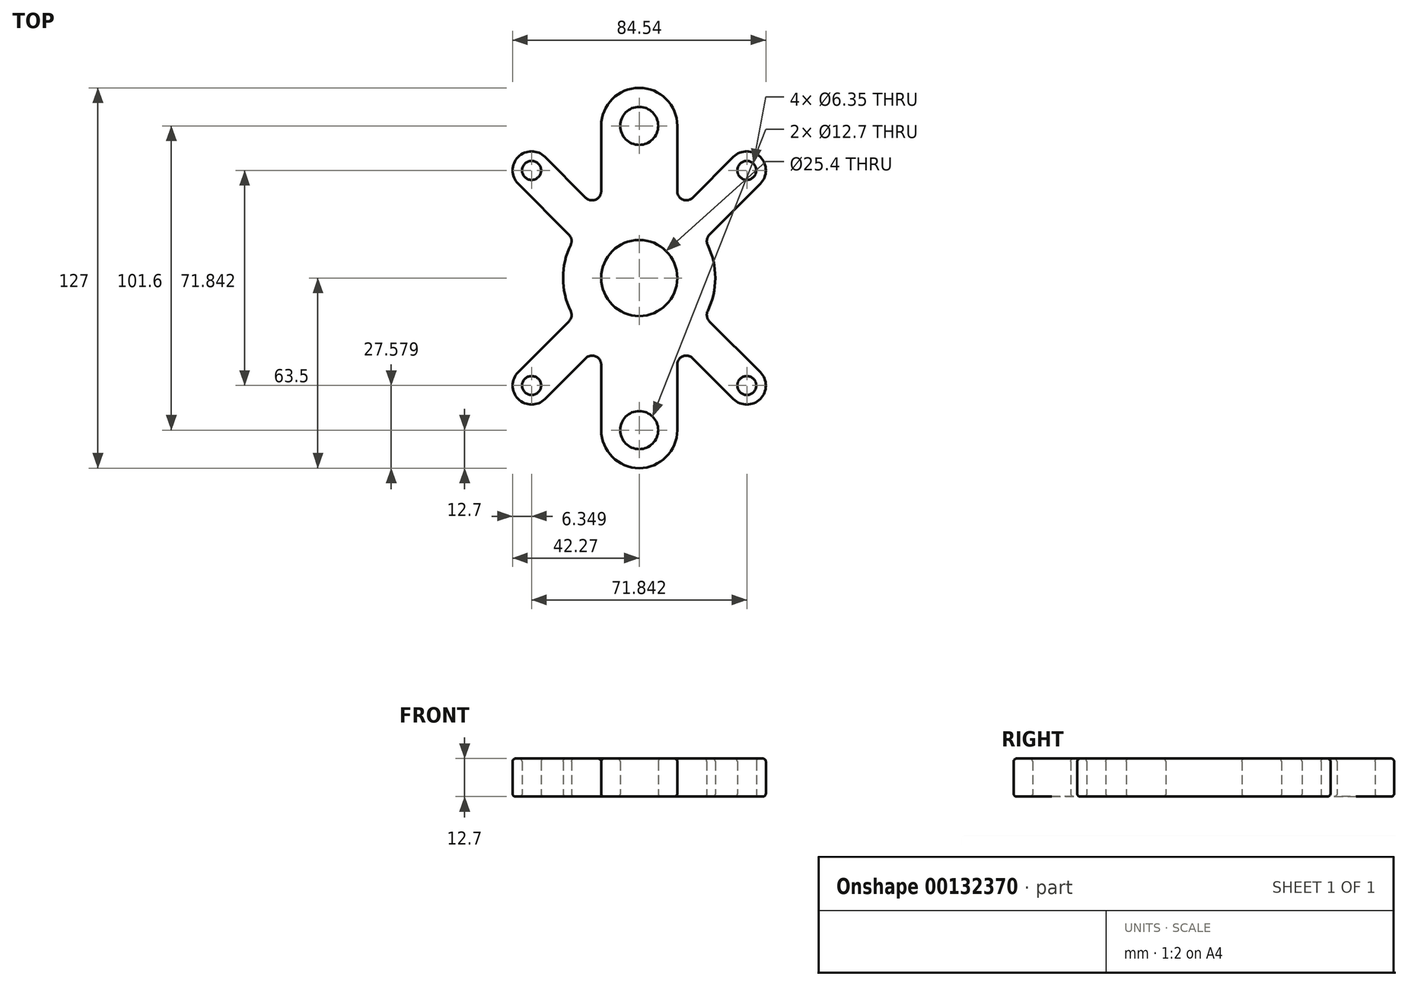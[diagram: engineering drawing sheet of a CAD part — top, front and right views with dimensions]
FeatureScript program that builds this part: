
annotation { "Feature Type Name" : "Feature", "Feature Type Description" : "" }
export const myFeature = defineFeature(function(context is Context, id is Id, definition is map)
    precondition{}
    {
        {
            var Q0;
            Q0=qCreatedBy(makeId("Top.planeOp"),FACE);
            var sketch = newSketch(context, id + "F0", { "sketchPlane" : qUnion([Q0])});
            skArc(sketch, "E0", {"start": v(-12.7, 22) * mm, "mid": v(-12.8, 21.94) * mm, "end": v(-12.9, 21.88) * mm});
            skCircle(sketch, "E1", {"center": v(0, 0) * mm, "radius": 12.7 * mm});
            skLineSegment(sketch, "E2", {"start": v(0, 0) * mm, "end": v(0, 50.8) * mm, "construction": true});
            skArc(sketch, "E3", {"start": v(12.7, 50.8) * mm, "mid": v(0, 63.5) * mm, "end": v(-12.7, 50.8) * mm});
            skCircle(sketch, "E4", {"center": v(0, 50.8) * mm, "radius": 6.35 * mm});
            skLineSegment(sketch, "E5", {"start": v(0, 0) * mm, "end": v(-35.92, 35.92) * mm, "construction": true});
            skLineSegment(sketch, "E6", {"start": v(35.92, -35.92) * mm, "end": v(0, 0) * mm, "construction": true});
            skLineSegment(sketch, "E7.MirrorCS", {"start": v(0, 0) * mm, "end": v(35.92, 35.92) * mm, "construction": true});
            skLineSegment(sketch, "E8.MirrorCS", {"start": v(-35.92, -35.92) * mm, "end": v(0, 0) * mm, "construction": true});
            skArc(sketch, "E9", {"start": v(-31.43, 40.41) * mm, "mid": v(-40.41, 40.41) * mm, "end": v(-40.41, 31.43) * mm});
            skArc(sketch, "E10", {"start": v(40.41, 31.43) * mm, "mid": v(40.41, 40.41) * mm, "end": v(31.43, 40.41) * mm});
            skArc(sketch, "E11", {"start": v(31.43, -40.41) * mm, "mid": v(40.41, -40.41) * mm, "end": v(40.41, -31.43) * mm});
            skArc(sketch, "E12", {"start": v(-40.41, -31.43) * mm, "mid": v(-40.41, -40.41) * mm, "end": v(-31.43, -40.41) * mm});
            skCircle(sketch, "E13", {"center": v(-35.92, 35.92) * mm, "radius": 3.17 * mm});
            skCircle(sketch, "E14", {"center": v(35.92, 35.92) * mm, "radius": 3.17 * mm});
            skCircle(sketch, "E15", {"center": v(35.92, -35.92) * mm, "radius": 3.17 * mm});
            skCircle(sketch, "E16", {"center": v(-35.92, -35.92) * mm, "radius": 3.17 * mm});
            skLineSegment(sketch, "E17", {"start": v(-12.7, 50.8) * mm, "end": v(-12.7, 28.92) * mm});
            skLineSegment(sketch, "E18", {"start": v(12.7, 50.8) * mm, "end": v(12.7, 28.92) * mm});
            skLineSegment(sketch, "E19", {"start": v(31.43, 40.41) * mm, "end": v(17.82, 26.8) * mm});
            skLineSegment(sketch, "E20", {"start": v(40.41, 31.43) * mm, "end": v(23.45, 14.47) * mm});
            skLineSegment(sketch, "E21", {"start": v(-31.43, 40.41) * mm, "end": v(-17.82, 26.8) * mm});
            skLineSegment(sketch, "E22", {"start": v(-40.41, 31.43) * mm, "end": v(-23.45, 14.47) * mm});
            skLineSegment(sketch, "E23", {"start": v(-31.43, -40.41) * mm, "end": v(-17.82, -26.8) * mm});
            skLineSegment(sketch, "E24", {"start": v(-40.41, -31.43) * mm, "end": v(-23.45, -14.47) * mm});
            skLineSegment(sketch, "E25", {"start": v(31.43, -40.41) * mm, "end": v(17.82, -26.8) * mm});
            skLineSegment(sketch, "E26", {"start": v(40.41, -31.43) * mm, "end": v(23.45, -14.47) * mm});
            skArc(sketch, "E27.trimOffspring", {"start": v(12.9, 21.88) * mm, "mid": v(12.8, 21.94) * mm, "end": v(12.7, 22) * mm});
            skArc(sketch, "E28.trimOffspring", {"start": v(-22.87, 11.05) * mm, "mid": v(-25.4, 0) * mm, "end": v(-22.87, -11.05) * mm});
            skArc(sketch, "E29.trimOffspring", {"start": v(22.87, -11.05) * mm, "mid": v(25.4, 0) * mm, "end": v(22.87, 11.05) * mm});
            skArc(sketch, "E30.filletArc", {"start": v(-17.82, 26.8) * mm, "mid": v(-14.55, 26.15) * mm, "end": v(-12.7, 28.92) * mm});
            skPoint(sketch, "E31.visualSharp", {"position": v(-21.88, 12.9) * mm});
            skArc(sketch, "E31.filletArc", {"start": v(-22.87, 11.05) * mm, "mid": v(-22.62, 12.85) * mm, "end": v(-23.45, 14.47) * mm});
            skArc(sketch, "E32.filletArc", {"start": v(12.7, 28.92) * mm, "mid": v(14.55, 26.15) * mm, "end": v(17.82, 26.8) * mm});
            skPoint(sketch, "E33.visualSharp", {"position": v(21.88, 12.9) * mm});
            skArc(sketch, "E33.filletArc", {"start": v(23.45, 14.47) * mm, "mid": v(22.62, 12.85) * mm, "end": v(22.87, 11.05) * mm});
            skPoint(sketch, "E34.visualSharp", {"position": v(21.88, -12.9) * mm});
            skArc(sketch, "E34.filletArc", {"start": v(22.87, -11.05) * mm, "mid": v(22.62, -12.85) * mm, "end": v(23.45, -14.47) * mm});
            skPoint(sketch, "E35.visualSharp", {"position": v(12.9, -21.88) * mm});
            skPoint(sketch, "E36.visualSharp", {"position": v(-12.9, -21.88) * mm});
            skPoint(sketch, "E37.visualSharp", {"position": v(-21.88, -12.9) * mm});
            skArc(sketch, "E37.filletArc", {"start": v(-23.45, -14.47) * mm, "mid": v(-22.62, -12.85) * mm, "end": v(-22.87, -11.05) * mm});
            skLineSegment(sketch, "E38", {"start": v(-25.4, 0) * mm, "end": v(25.4, 0) * mm, "construction": true});
            skArc(sketch, "E39.MirrorCS", {"start": v(12.7, -50.8) * mm, "mid": v(0, -63.5) * mm, "end": v(-12.7, -50.8) * mm});
            skCircle(sketch, "E40.MirrorC", {"center": v(0, -50.8) * mm, "radius": 6.35 * mm});
            skLineSegment(sketch, "E41.MirrorCS", {"start": v(0, 0) * mm, "end": v(0, -50.8) * mm, "construction": true});
            skLineSegment(sketch, "E42", {"start": v(-12.7, -50.8) * mm, "end": v(-12.7, -28.92) * mm});
            skLineSegment(sketch, "E43", {"start": v(12.7, -50.8) * mm, "end": v(12.7, -28.92) * mm});
            skArc(sketch, "E44.filletArc", {"start": v(-12.7, -28.92) * mm, "mid": v(-14.55, -26.15) * mm, "end": v(-17.82, -26.8) * mm});
            skArc(sketch, "E45.filletArc", {"start": v(17.82, -26.8) * mm, "mid": v(14.55, -26.15) * mm, "end": v(12.7, -28.92) * mm});
            skSolve(sketch);
        }
        {
            var Q0;
            Q0=makeQuery(id+"F0.imprint","IMPRINT",FACE,{"disambiguationData":[TD([[makeQuery(id+"F0.imprint","IMPRINT",EDGE,{"derivedFrom":sQuery(id+"F0.wireOp",EDGE,"E1")}),-1.0]])]});
            extrude(context, id + "F1", {"entities" : qUnion([Q0]), "depth" : 12.7 * mm});
        }
        {
            var Q0;
            Q0=makeQuery(id+"F1.opExtrude","CAP_FACE",FACE,{"disambiguationData":[OSD([sQuery(id+"F0.wireOp",EDGE,"E1"),sQuery(id+"F0.wireOp",EDGE,"E3"),sQuery(id+"F0.wireOp",EDGE,"E4"),sQuery(id+"F0.wireOp",EDGE,"E9"),sQuery(id+"F0.wireOp",EDGE,"E10"),sQuery(id+"F0.wireOp",EDGE,"E11"),sQuery(id+"F0.wireOp",EDGE,"E12"),sQuery(id+"F0.wireOp",EDGE,"E13"),sQuery(id+"F0.wireOp",EDGE,"E14"),sQuery(id+"F0.wireOp",EDGE,"E15"),sQuery(id+"F0.wireOp",EDGE,"E16"),sQuery(id+"F0.wireOp",EDGE,"E17"),sQuery(id+"F0.wireOp",EDGE,"E18"),sQuery(id+"F0.wireOp",EDGE,"E19"),sQuery(id+"F0.wireOp",EDGE,"E20"),sQuery(id+"F0.wireOp",EDGE,"E21"),sQuery(id+"F0.wireOp",EDGE,"E22"),sQuery(id+"F0.wireOp",EDGE,"E23"),sQuery(id+"F0.wireOp",EDGE,"E24"),sQuery(id+"F0.wireOp",EDGE,"E25"),sQuery(id+"F0.wireOp",EDGE,"E26"),sQuery(id+"F0.wireOp",EDGE,"E28.trimOffspring"),sQuery(id+"F0.wireOp",EDGE,"E29.trimOffspring"),sQuery(id+"F0.wireOp",EDGE,"E30.filletArc"),sQuery(id+"F0.wireOp",EDGE,"E31.filletArc"),sQuery(id+"F0.wireOp",EDGE,"E32.filletArc"),sQuery(id+"F0.wireOp",EDGE,"E33.filletArc"),sQuery(id+"F0.wireOp",EDGE,"E34.filletArc"),sQuery(id+"F0.wireOp",EDGE,"E37.filletArc"),sQuery(id+"F0.wireOp",EDGE,"E39.MirrorCS"),sQuery(id+"F0.wireOp",EDGE,"E40.MirrorC"),sQuery(id+"F0.wireOp",EDGE,"E42"),sQuery(id+"F0.wireOp",EDGE,"E43"),sQuery(id+"F0.wireOp",EDGE,"E44.filletArc"),sQuery(id+"F0.wireOp",EDGE,"E45.filletArc")])],"isStart":false});
            var Q1;
            Q1=makeQuery(id+"F1.opExtrude","SWEPT_FACE",FACE,{"disambiguationData":[OSD([sQuery(id+"F0.wireOp",EDGE,"E43")])]});
            var Q2;
            Q2=makeQuery(id+"F1.opExtrude","SWEPT_FACE",FACE,{"disambiguationData":[OSD([sQuery(id+"F0.wireOp",EDGE,"E39.MirrorCS")])]});
            var Q3;
            Q3=makeQuery(id+"F1.opExtrude","SWEPT_FACE",FACE,{"disambiguationData":[OSD([sQuery(id+"F0.wireOp",EDGE,"E44.filletArc")])]});
            var Q4;
            Q4=makeQuery(id+"F1.opExtrude","SWEPT_FACE",FACE,{"disambiguationData":[OSD([sQuery(id+"F0.wireOp",EDGE,"E30.filletArc")])]});
            var Q5;
            Q5=makeQuery(id+"F1.opExtrude","CAP_EDGE",EDGE,{"disambiguationData":[OSD([sQuery(id+"F0.wireOp",EDGE,"E25")])],"isStart":false});
            var Q6;
            Q6=makeQuery(id+"F1.opExtrude","CAP_EDGE",EDGE,{"disambiguationData":[OSD([sQuery(id+"F0.wireOp",EDGE,"E25")])],"isStart":true});
            var Q7;
            Q7=makeQuery(id+"F1.opExtrude","CAP_EDGE",EDGE,{"disambiguationData":[OSD([sQuery(id+"F0.wireOp",EDGE,"E17")])],"isStart":false});
            var Q8;
            Q8=makeQuery(id+"F1.opExtrude","SWEPT_FACE",FACE,{"disambiguationData":[OSD([sQuery(id+"F0.wireOp",EDGE,"E23")])]});
            var Q9;
            Q9=makeQuery(id+"F1.opExtrude","CAP_EDGE",EDGE,{"disambiguationData":[OSD([sQuery(id+"F0.wireOp",EDGE,"E39.MirrorCS")])],"isStart":true});
            var Q10;
            Q10=makeQuery(id+"F1.opExtrude","CAP_EDGE",EDGE,{"disambiguationData":[OSD([sQuery(id+"F0.wireOp",EDGE,"E3")])],"isStart":false});
            var Q11;
            Q11=makeQuery(id+"F1.opExtrude","SWEPT_FACE",FACE,{"disambiguationData":[OSD([sQuery(id+"F0.wireOp",EDGE,"E22")])]});
            var Q12;
            Q12=makeQuery(id+"F1.opExtrude","CAP_EDGE",EDGE,{"disambiguationData":[OSD([sQuery(id+"F0.wireOp",EDGE,"E20")])],"isStart":false});
            var Q13;
            Q13=makeQuery(id+"F1.opExtrude","CAP_EDGE",EDGE,{"disambiguationData":[OSD([sQuery(id+"F0.wireOp",EDGE,"E29.trimOffspring")])],"isStart":false});
            var Q14;
            Q14=makeQuery(id+"F1.opExtrude","SWEPT_FACE",FACE,{"disambiguationData":[OSD([sQuery(id+"F0.wireOp",EDGE,"E29.trimOffspring")])]});
            var Q15;
            Q15=makeQuery(id+"F1.opExtrude","SWEPT_FACE",FACE,{"disambiguationData":[OSD([sQuery(id+"F0.wireOp",EDGE,"E33.filletArc")])]});
            var Q16;
            Q16=makeQuery(id+"F1.opExtrude","SWEPT_FACE",FACE,{"disambiguationData":[OSD([sQuery(id+"F0.wireOp",EDGE,"E16")])]});
            var Q17;
            Q17=makeQuery(id+"F1.opExtrude","CAP_EDGE",EDGE,{"disambiguationData":[OSD([sQuery(id+"F0.wireOp",EDGE,"E4")])],"isStart":false});
            var Q18;
            Q18=makeQuery(id+"F1.opExtrude","SWEPT_FACE",FACE,{"disambiguationData":[OSD([sQuery(id+"F0.wireOp",EDGE,"E15")])]});
            var Q19;
            Q19=makeQuery(id+"F1.opExtrude","SWEPT_FACE",FACE,{"disambiguationData":[OSD([sQuery(id+"F0.wireOp",EDGE,"E14")])]});
            var Q20;
            Q20=makeQuery(id+"F1.opExtrude","CAP_EDGE",EDGE,{"disambiguationData":[OSD([sQuery(id+"F0.wireOp",EDGE,"E26")])],"isStart":false});
            var Q21;
            Q21=makeQuery(id+"F1.opExtrude","SWEPT_FACE",FACE,{"disambiguationData":[OSD([sQuery(id+"F0.wireOp",EDGE,"E13")])]});
            var Q22;
            Q22=makeQuery(id+"F1.opExtrude","SWEPT_FACE",FACE,{"disambiguationData":[OSD([sQuery(id+"F0.wireOp",EDGE,"E12")])]});
            var Q23;
            Q23=makeQuery(id+"F1.opExtrude","CAP_EDGE",EDGE,{"disambiguationData":[OSD([sQuery(id+"F0.wireOp",EDGE,"E18")])],"isStart":false});
            var Q24;
            Q24=makeQuery(id+"F1.opExtrude","SWEPT_FACE",FACE,{"disambiguationData":[OSD([sQuery(id+"F0.wireOp",EDGE,"E11")])]});
            var Q25;
            Q25=makeQuery(id+"F1.opExtrude","SWEPT_FACE",FACE,{"disambiguationData":[OSD([sQuery(id+"F0.wireOp",EDGE,"E10")])]});
            var Q26;
            Q26=makeQuery(id+"F1.opExtrude","SWEPT_FACE",FACE,{"disambiguationData":[OSD([sQuery(id+"F0.wireOp",EDGE,"E21")])]});
            var Q27;
            Q27=makeQuery(id+"F1.opExtrude","CAP_EDGE",EDGE,{"disambiguationData":[OSD([sQuery(id+"F0.wireOp",EDGE,"E20")])],"isStart":true});
            var Q28;
            Q28=makeQuery(id+"F1.opExtrude","SWEPT_FACE",FACE,{"disambiguationData":[OSD([sQuery(id+"F0.wireOp",EDGE,"E9")])]});
            var Q29;
            Q29=makeQuery(id+"F1.opExtrude","SWEPT_FACE",FACE,{"disambiguationData":[OSD([sQuery(id+"F0.wireOp",EDGE,"E4")])]});
            var Q30;
            Q30=makeQuery(id+"F1.opExtrude","SWEPT_FACE",FACE,{"disambiguationData":[OSD([sQuery(id+"F0.wireOp",EDGE,"E3")])]});
            var Q31;
            Q31=makeQuery(id+"F1.opExtrude","SWEPT_FACE",FACE,{"disambiguationData":[OSD([sQuery(id+"F0.wireOp",EDGE,"E25")])]});
            var Q32;
            Q32=makeQuery(id+"F1.opExtrude","SWEPT_FACE",FACE,{"disambiguationData":[OSD([sQuery(id+"F0.wireOp",EDGE,"E37.filletArc")])]});
            var Q33;
            Q33=makeQuery(id+"F1.opExtrude","CAP_FACE",FACE,{"disambiguationData":[OSD([sQuery(id+"F0.wireOp",EDGE,"E1"),sQuery(id+"F0.wireOp",EDGE,"E3"),sQuery(id+"F0.wireOp",EDGE,"E4"),sQuery(id+"F0.wireOp",EDGE,"E9"),sQuery(id+"F0.wireOp",EDGE,"E10"),sQuery(id+"F0.wireOp",EDGE,"E11"),sQuery(id+"F0.wireOp",EDGE,"E12"),sQuery(id+"F0.wireOp",EDGE,"E13"),sQuery(id+"F0.wireOp",EDGE,"E14"),sQuery(id+"F0.wireOp",EDGE,"E15"),sQuery(id+"F0.wireOp",EDGE,"E16"),sQuery(id+"F0.wireOp",EDGE,"E17"),sQuery(id+"F0.wireOp",EDGE,"E18"),sQuery(id+"F0.wireOp",EDGE,"E19"),sQuery(id+"F0.wireOp",EDGE,"E20"),sQuery(id+"F0.wireOp",EDGE,"E21"),sQuery(id+"F0.wireOp",EDGE,"E22"),sQuery(id+"F0.wireOp",EDGE,"E23"),sQuery(id+"F0.wireOp",EDGE,"E24"),sQuery(id+"F0.wireOp",EDGE,"E25"),sQuery(id+"F0.wireOp",EDGE,"E26"),sQuery(id+"F0.wireOp",EDGE,"E28.trimOffspring"),sQuery(id+"F0.wireOp",EDGE,"E29.trimOffspring"),sQuery(id+"F0.wireOp",EDGE,"E30.filletArc"),sQuery(id+"F0.wireOp",EDGE,"E31.filletArc"),sQuery(id+"F0.wireOp",EDGE,"E32.filletArc"),sQuery(id+"F0.wireOp",EDGE,"E33.filletArc"),sQuery(id+"F0.wireOp",EDGE,"E34.filletArc"),sQuery(id+"F0.wireOp",EDGE,"E37.filletArc"),sQuery(id+"F0.wireOp",EDGE,"E39.MirrorCS"),sQuery(id+"F0.wireOp",EDGE,"E40.MirrorC"),sQuery(id+"F0.wireOp",EDGE,"E42"),sQuery(id+"F0.wireOp",EDGE,"E43"),sQuery(id+"F0.wireOp",EDGE,"E44.filletArc"),sQuery(id+"F0.wireOp",EDGE,"E45.filletArc")])],"isStart":true});
            var Q34;
            Q34=makeQuery(id+"F1.opExtrude","CAP_EDGE",EDGE,{"disambiguationData":[OSD([sQuery(id+"F0.wireOp",EDGE,"E43")])],"isStart":true});
            var Q35;
            Q35=makeQuery(id+"F1.opExtrude","SWEPT_FACE",FACE,{"disambiguationData":[OSD([sQuery(id+"F0.wireOp",EDGE,"E1")])]});
            var Q36;
            Q36=makeQuery(id+"F1.opExtrude","CAP_EDGE",EDGE,{"disambiguationData":[OSD([sQuery(id+"F0.wireOp",EDGE,"E1")])],"isStart":true});
            var Q37;
            Q37=makeQuery(id+"F1.opExtrude","SWEPT_FACE",FACE,{"disambiguationData":[OSD([sQuery(id+"F0.wireOp",EDGE,"E28.trimOffspring")])]});
            var Q38;
            Q38=makeQuery(id+"F1.opExtrude","SWEPT_FACE",FACE,{"disambiguationData":[OSD([sQuery(id+"F0.wireOp",EDGE,"E18")])]});
            var Q39;
            Q39=makeQuery(id+"F1.opExtrude","SWEPT_FACE",FACE,{"disambiguationData":[OSD([sQuery(id+"F0.wireOp",EDGE,"E17")])]});
            var Q40;
            Q40=makeQuery(id+"F1.opExtrude","SWEPT_FACE",FACE,{"disambiguationData":[OSD([sQuery(id+"F0.wireOp",EDGE,"E19")])]});
            var Q41;
            Q41=makeQuery(id+"F1.opExtrude","SWEPT_FACE",FACE,{"disambiguationData":[OSD([sQuery(id+"F0.wireOp",EDGE,"E32.filletArc")])]});
            var Q42;
            Q42=makeQuery(id+"F1.opExtrude","CAP_EDGE",EDGE,{"disambiguationData":[OSD([sQuery(id+"F0.wireOp",EDGE,"E22")])],"isStart":false});
            var Q43;
            Q43=makeQuery(id+"F1.opExtrude","CAP_EDGE",EDGE,{"disambiguationData":[OSD([sQuery(id+"F0.wireOp",EDGE,"E43")])],"isStart":false});
            var Q44;
            Q44=makeQuery(id+"F1.opExtrude","CAP_EDGE",EDGE,{"disambiguationData":[OSD([sQuery(id+"F0.wireOp",EDGE,"E1")])],"isStart":false});
            var Q45;
            Q45=makeQuery(id+"F1.opExtrude","SWEPT_FACE",FACE,{"disambiguationData":[OSD([sQuery(id+"F0.wireOp",EDGE,"E20")])]});
            var Q46;
            Q46=makeQuery(id+"F1.opExtrude","SWEPT_FACE",FACE,{"disambiguationData":[OSD([sQuery(id+"F0.wireOp",EDGE,"E40.MirrorC")])]});
            var Q47;
            Q47=makeQuery(id+"F1.opExtrude","CAP_EDGE",EDGE,{"disambiguationData":[OSD([sQuery(id+"F0.wireOp",EDGE,"E28.trimOffspring")])],"isStart":false});
            var Q48;
            Q48=makeQuery(id+"F1.opExtrude","CAP_EDGE",EDGE,{"disambiguationData":[OSD([sQuery(id+"F0.wireOp",EDGE,"E39.MirrorCS")])],"isStart":false});
            var Q49;
            Q49=makeQuery(id+"F1.opExtrude","SWEPT_FACE",FACE,{"disambiguationData":[OSD([sQuery(id+"F0.wireOp",EDGE,"E24")])]});
            var Q50;
            Q50=makeQuery(id+"F1.opExtrude","CAP_EDGE",EDGE,{"disambiguationData":[OSD([sQuery(id+"F0.wireOp",EDGE,"E21")])],"isStart":false});
            var Q51;
            Q51=makeQuery(id+"F1.opExtrude","SWEPT_FACE",FACE,{"disambiguationData":[OSD([sQuery(id+"F0.wireOp",EDGE,"E45.filletArc")])]});
            var Q52;
            Q52=makeQuery(id+"F1.opExtrude","CAP_EDGE",EDGE,{"disambiguationData":[OSD([sQuery(id+"F0.wireOp",EDGE,"E42")])],"isStart":false});
            var Q53;
            Q53=makeQuery(id+"F1.opExtrude","SWEPT_FACE",FACE,{"disambiguationData":[OSD([sQuery(id+"F0.wireOp",EDGE,"E26")])]});
            var Q54;
            Q54=makeQuery(id+"F1.opExtrude","SWEPT_EDGE",EDGE,{"disambiguationData":[OSD([sQuery(id+"F0.wireOp",EDGE,"E25"),sQuery(id+"F0.wireOp",EDGE,"E45.filletArc")])]});
            var Q55;
            Q55=makeQuery(id+"F1.opExtrude","CAP_EDGE",EDGE,{"disambiguationData":[OSD([sQuery(id+"F0.wireOp",EDGE,"E28.trimOffspring")])],"isStart":true});
            var Q56;
            Q56=makeQuery(id+"F1.opExtrude","CAP_EDGE",EDGE,{"disambiguationData":[OSD([sQuery(id+"F0.wireOp",EDGE,"E13")])],"isStart":true});
            var Q57;
            Q57=makeQuery(id+"F1.opExtrude","CAP_EDGE",EDGE,{"disambiguationData":[OSD([sQuery(id+"F0.wireOp",EDGE,"E42")])],"isStart":true});
            var Q58;
            Q58=makeQuery(id+"F1.opExtrude","CAP_EDGE",EDGE,{"disambiguationData":[OSD([sQuery(id+"F0.wireOp",EDGE,"E9")])],"isStart":true});
            var Q59;
            Q59=makeQuery(id+"F1.opExtrude","CAP_EDGE",EDGE,{"disambiguationData":[OSD([sQuery(id+"F0.wireOp",EDGE,"E17")])],"isStart":true});
            var Q60;
            Q60=makeQuery(id+"F1.opExtrude","CAP_EDGE",EDGE,{"disambiguationData":[OSD([sQuery(id+"F0.wireOp",EDGE,"E23")])],"isStart":false});
            var Q61;
            Q61=makeQuery(id+"F1.opExtrude","CAP_EDGE",EDGE,{"disambiguationData":[OSD([sQuery(id+"F0.wireOp",EDGE,"E9")])],"isStart":false});
            var Q62;
            Q62=makeQuery(id+"F1.opExtrude","CAP_EDGE",EDGE,{"disambiguationData":[OSD([sQuery(id+"F0.wireOp",EDGE,"E21")])],"isStart":true});
            var Q63;
            Q63=makeQuery(id+"F1.opExtrude","CAP_EDGE",EDGE,{"disambiguationData":[OSD([sQuery(id+"F0.wireOp",EDGE,"E30.filletArc")])],"isStart":true});
            var Q64;
            Q64=makeQuery(id+"F1.opExtrude","CAP_EDGE",EDGE,{"disambiguationData":[OSD([sQuery(id+"F0.wireOp",EDGE,"E32.filletArc")])],"isStart":false});
            var Q65;
            Q65=makeQuery(id+"F1.opExtrude","CAP_EDGE",EDGE,{"disambiguationData":[OSD([sQuery(id+"F0.wireOp",EDGE,"E44.filletArc")])],"isStart":false});
            var Q66;
            Q66=makeQuery(id+"F1.opExtrude","CAP_EDGE",EDGE,{"disambiguationData":[OSD([sQuery(id+"F0.wireOp",EDGE,"E11")])],"isStart":true});
            var Q67;
            Q67=makeQuery(id+"F1.opExtrude","CAP_EDGE",EDGE,{"disambiguationData":[OSD([sQuery(id+"F0.wireOp",EDGE,"E15")])],"isStart":false});
            var Q68;
            Q68=makeQuery(id+"F1.opExtrude","CAP_EDGE",EDGE,{"disambiguationData":[OSD([sQuery(id+"F0.wireOp",EDGE,"E19")])],"isStart":true});
            var Q69;
            Q69=makeQuery(id+"F1.opExtrude","CAP_EDGE",EDGE,{"disambiguationData":[OSD([sQuery(id+"F0.wireOp",EDGE,"E12")])],"isStart":false});
            var Q70;
            Q70=makeQuery(id+"F1.opExtrude","CAP_EDGE",EDGE,{"disambiguationData":[OSD([sQuery(id+"F0.wireOp",EDGE,"E40.MirrorC")])],"isStart":false});
            var Q71;
            Q71=makeQuery(id+"F1.opExtrude","CAP_EDGE",EDGE,{"disambiguationData":[OSD([sQuery(id+"F0.wireOp",EDGE,"E24")])],"isStart":false});
            var Q72;
            Q72=makeQuery(id+"F1.opExtrude","CAP_EDGE",EDGE,{"disambiguationData":[OSD([sQuery(id+"F0.wireOp",EDGE,"E33.filletArc")])],"isStart":false});
            var Q73;
            Q73=makeQuery(id+"F1.opExtrude","CAP_EDGE",EDGE,{"disambiguationData":[OSD([sQuery(id+"F0.wireOp",EDGE,"E45.filletArc")])],"isStart":false});
            var Q74;
            Q74=makeQuery(id+"F1.opExtrude","SWEPT_EDGE",EDGE,{"disambiguationData":[OSD([sQuery(id+"F0.wireOp",EDGE,"E19"),sQuery(id+"F0.wireOp",EDGE,"E32.filletArc")])]});
            var Q75;
            Q75=makeQuery(id+"F1.opExtrude","SWEPT_EDGE",EDGE,{"disambiguationData":[OSD([sQuery(id+"F0.wireOp",EDGE,"E24"),sQuery(id+"F0.wireOp",EDGE,"E37.filletArc")])]});
            var Q76;
            Q76=makeQuery(id+"F1.opExtrude","CAP_EDGE",EDGE,{"disambiguationData":[OSD([sQuery(id+"F0.wireOp",EDGE,"E16")])],"isStart":false});
            var Q77;
            Q77=makeQuery(id+"F1.opExtrude","SWEPT_EDGE",EDGE,{"disambiguationData":[OSD([sQuery(id+"F0.wireOp",EDGE,"E18"),sQuery(id+"F0.wireOp",EDGE,"E32.filletArc")])]});
            var Q78;
            Q78=makeQuery(id+"F1.opExtrude","SWEPT_EDGE",EDGE,{"disambiguationData":[OSD([sQuery(id+"F0.wireOp",EDGE,"E17"),sQuery(id+"F0.wireOp",EDGE,"E30.filletArc")])]});
            var Q79;
            Q79=makeQuery(id+"F1.opExtrude","CAP_EDGE",EDGE,{"disambiguationData":[OSD([sQuery(id+"F0.wireOp",EDGE,"E23")])],"isStart":true});
            var Q80;
            Q80=makeQuery(id+"F1.opExtrude","SWEPT_EDGE",EDGE,{"disambiguationData":[OSD([sQuery(id+"F0.wireOp",EDGE,"E12"),sQuery(id+"F0.wireOp",EDGE,"E23")])]});
            var Q81;
            Q81=makeQuery(id+"F1.opExtrude","CAP_EDGE",EDGE,{"disambiguationData":[OSD([sQuery(id+"F0.wireOp",EDGE,"E37.filletArc")])],"isStart":false});
            var Q82;
            Q82=makeQuery(id+"F1.opExtrude","CAP_EDGE",EDGE,{"disambiguationData":[OSD([sQuery(id+"F0.wireOp",EDGE,"E32.filletArc")])],"isStart":true});
            var Q83;
            Q83=makeQuery(id+"F1.opExtrude","SWEPT_EDGE",EDGE,{"disambiguationData":[OSD([sQuery(id+"F0.wireOp",EDGE,"E12"),sQuery(id+"F0.wireOp",EDGE,"E24")])]});
            var Q84;
            Q84=makeQuery(id+"F1.opExtrude","SWEPT_EDGE",EDGE,{"disambiguationData":[OSD([sQuery(id+"F0.wireOp",EDGE,"E28.trimOffspring"),sQuery(id+"F0.wireOp",EDGE,"E37.filletArc")])]});
            var Q85;
            Q85=makeQuery(id+"F1.opExtrude","CAP_EDGE",EDGE,{"disambiguationData":[OSD([sQuery(id+"F0.wireOp",EDGE,"E10")])],"isStart":false});
            var Q86;
            Q86=makeQuery(id+"F1.opExtrude","CAP_EDGE",EDGE,{"disambiguationData":[OSD([sQuery(id+"F0.wireOp",EDGE,"E3")])],"isStart":true});
            var Q87;
            Q87=makeQuery(id+"F1.opExtrude","CAP_EDGE",EDGE,{"disambiguationData":[OSD([sQuery(id+"F0.wireOp",EDGE,"E15")])],"isStart":true});
            var Q88;
            Q88=makeQuery(id+"F1.opExtrude","SWEPT_EDGE",EDGE,{"disambiguationData":[OSD([sQuery(id+"F0.wireOp",EDGE,"E11"),sQuery(id+"F0.wireOp",EDGE,"E26")])]});
            var Q89;
            Q89=makeQuery(id+"F1.opExtrude","SWEPT_EDGE",EDGE,{"disambiguationData":[OSD([sQuery(id+"F0.wireOp",EDGE,"E11"),sQuery(id+"F0.wireOp",EDGE,"E25")])]});
            var Q90;
            Q90=makeQuery(id+"F1.opExtrude","CAP_EDGE",EDGE,{"disambiguationData":[OSD([sQuery(id+"F0.wireOp",EDGE,"E12")])],"isStart":true});
            var Q91;
            Q91=makeQuery(id+"F1.opExtrude","SWEPT_FACE",FACE,{"disambiguationData":[OSD([sQuery(id+"F0.wireOp",EDGE,"E42")])]});
            var Q92;
            Q92=makeQuery(id+"F1.opExtrude","SWEPT_EDGE",EDGE,{"disambiguationData":[OSD([sQuery(id+"F0.wireOp",EDGE,"E10"),sQuery(id+"F0.wireOp",EDGE,"E19")])]});
            var Q93;
            Q93=makeQuery(id+"F1.opExtrude","CAP_EDGE",EDGE,{"disambiguationData":[OSD([sQuery(id+"F0.wireOp",EDGE,"E29.trimOffspring")])],"isStart":true});
            var Q94;
            Q94=makeQuery(id+"F1.opExtrude","CAP_EDGE",EDGE,{"disambiguationData":[OSD([sQuery(id+"F0.wireOp",EDGE,"E40.MirrorC")])],"isStart":true});
            var Q95;
            Q95=makeQuery(id+"F1.opExtrude","SWEPT_EDGE",EDGE,{"disambiguationData":[OSD([sQuery(id+"F0.wireOp",EDGE,"E10"),sQuery(id+"F0.wireOp",EDGE,"E20")])]});
            var Q96;
            Q96=makeQuery(id+"F1.opExtrude","SWEPT_EDGE",EDGE,{"disambiguationData":[OSD([sQuery(id+"F0.wireOp",EDGE,"E39.MirrorCS"),sQuery(id+"F0.wireOp",EDGE,"E43")])]});
            var Q97;
            Q97=makeQuery(id+"F1.opExtrude","SWEPT_EDGE",EDGE,{"disambiguationData":[OSD([sQuery(id+"F0.wireOp",EDGE,"E9"),sQuery(id+"F0.wireOp",EDGE,"E22")])]});
            var Q98;
            Q98=makeQuery(id+"F1.opExtrude","SWEPT_EDGE",EDGE,{"disambiguationData":[OSD([sQuery(id+"F0.wireOp",EDGE,"E9"),sQuery(id+"F0.wireOp",EDGE,"E21")])]});
            var Q99;
            Q99=makeQuery(id+"F1.opExtrude","CAP_EDGE",EDGE,{"disambiguationData":[OSD([sQuery(id+"F0.wireOp",EDGE,"E14")])],"isStart":true});
            var Q100;
            Q100=makeQuery(id+"F1.opExtrude","CAP_EDGE",EDGE,{"disambiguationData":[OSD([sQuery(id+"F0.wireOp",EDGE,"E22")])],"isStart":true});
            var Q101;
            Q101=makeQuery(id+"F1.opExtrude","SWEPT_EDGE",EDGE,{"disambiguationData":[OSD([sQuery(id+"F0.wireOp",EDGE,"E3"),sQuery(id+"F0.wireOp",EDGE,"E17")])]});
            var Q102;
            Q102=makeQuery(id+"F1.opExtrude","SWEPT_EDGE",EDGE,{"disambiguationData":[OSD([sQuery(id+"F0.wireOp",EDGE,"E3"),sQuery(id+"F0.wireOp",EDGE,"E18")])]});
            var Q103;
            Q103=makeQuery(id+"F1.opExtrude","SWEPT_EDGE",EDGE,{"disambiguationData":[OSD([sQuery(id+"F0.wireOp",EDGE,"E21"),sQuery(id+"F0.wireOp",EDGE,"E30.filletArc")])]});
            var Q104;
            Q104=makeQuery(id+"F1.opExtrude","SWEPT_EDGE",EDGE,{"disambiguationData":[OSD([sQuery(id+"F0.wireOp",EDGE,"E20"),sQuery(id+"F0.wireOp",EDGE,"E33.filletArc")])]});
            var Q105;
            Q105=makeQuery(id+"F1.opExtrude","SWEPT_EDGE",EDGE,{"disambiguationData":[OSD([sQuery(id+"F0.wireOp",EDGE,"E23"),sQuery(id+"F0.wireOp",EDGE,"E44.filletArc")])]});
            var Q106;
            Q106=makeQuery(id+"F1.opExtrude","CAP_EDGE",EDGE,{"disambiguationData":[OSD([sQuery(id+"F0.wireOp",EDGE,"E4")])],"isStart":true});
            var Q107;
            Q107=makeQuery(id+"F1.opExtrude","CAP_EDGE",EDGE,{"disambiguationData":[OSD([sQuery(id+"F0.wireOp",EDGE,"E16")])],"isStart":true});
            var Q108;
            Q108=makeQuery(id+"F1.opExtrude","CAP_EDGE",EDGE,{"disambiguationData":[OSD([sQuery(id+"F0.wireOp",EDGE,"E26")])],"isStart":true});
            var Q109;
            Q109=makeQuery(id+"F1.opExtrude","CAP_EDGE",EDGE,{"disambiguationData":[OSD([sQuery(id+"F0.wireOp",EDGE,"E10")])],"isStart":true});
            var Q110;
            Q110=makeQuery(id+"F1.opExtrude","CAP_EDGE",EDGE,{"disambiguationData":[OSD([sQuery(id+"F0.wireOp",EDGE,"E18")])],"isStart":true});
            var Q111;
            Q111=makeQuery(id+"F1.opExtrude","CAP_EDGE",EDGE,{"disambiguationData":[OSD([sQuery(id+"F0.wireOp",EDGE,"E14")])],"isStart":false});
            var Q112;
            Q112=makeQuery(id+"F1.opExtrude","CAP_EDGE",EDGE,{"disambiguationData":[OSD([sQuery(id+"F0.wireOp",EDGE,"E11")])],"isStart":false});
            var Q113;
            Q113=makeQuery(id+"F1.opExtrude","CAP_EDGE",EDGE,{"disambiguationData":[OSD([sQuery(id+"F0.wireOp",EDGE,"E19")])],"isStart":false});
            var Q114;
            Q114=makeQuery(id+"F1.opExtrude","SWEPT_EDGE",EDGE,{"disambiguationData":[OSD([sQuery(id+"F0.wireOp",EDGE,"E29.trimOffspring"),sQuery(id+"F0.wireOp",EDGE,"E33.filletArc")])]});
            var Q115;
            Q115=makeQuery(id+"F1.opExtrude","CAP_EDGE",EDGE,{"disambiguationData":[OSD([sQuery(id+"F0.wireOp",EDGE,"E13")])],"isStart":false});
            var Q116;
            Q116=makeQuery(id+"F1.opExtrude","SWEPT_FACE",FACE,{"disambiguationData":[OSD([sQuery(id+"F0.wireOp",EDGE,"E34.filletArc")])]});
            var Q117;
            Q117=makeQuery(id+"F1.opExtrude","CAP_EDGE",EDGE,{"disambiguationData":[OSD([sQuery(id+"F0.wireOp",EDGE,"E30.filletArc")])],"isStart":false});
            var Q118;
            Q118=makeQuery(id+"F1.opExtrude","SWEPT_EDGE",EDGE,{"disambiguationData":[OSD([sQuery(id+"F0.wireOp",EDGE,"E43"),sQuery(id+"F0.wireOp",EDGE,"E45.filletArc")])]});
            var Q119;
            Q119=makeQuery(id+"F1.opExtrude","CAP_EDGE",EDGE,{"disambiguationData":[OSD([sQuery(id+"F0.wireOp",EDGE,"E24")])],"isStart":true});
            var Q120;
            Q120=makeQuery(id+"F1.opExtrude","CAP_EDGE",EDGE,{"disambiguationData":[OSD([sQuery(id+"F0.wireOp",EDGE,"E33.filletArc")])],"isStart":true});
            var Q121;
            Q121=makeQuery(id+"F1.opExtrude","CAP_EDGE",EDGE,{"disambiguationData":[OSD([sQuery(id+"F0.wireOp",EDGE,"E45.filletArc")])],"isStart":true});
            var Q122;
            Q122=makeQuery(id+"F1.opExtrude","SWEPT_FACE",FACE,{"disambiguationData":[OSD([sQuery(id+"F0.wireOp",EDGE,"E31.filletArc")])]});
            var Q123;
            Q123=makeQuery(id+"F1.opExtrude","CAP_EDGE",EDGE,{"disambiguationData":[OSD([sQuery(id+"F0.wireOp",EDGE,"E34.filletArc")])],"isStart":false});
            var Q124;
            Q124=makeQuery(id+"F1.opExtrude","SWEPT_EDGE",EDGE,{"disambiguationData":[OSD([sQuery(id+"F0.wireOp",EDGE,"E42"),sQuery(id+"F0.wireOp",EDGE,"E44.filletArc")])]});
            var Q125;
            Q125=makeQuery(id+"F1.opExtrude","CAP_EDGE",EDGE,{"disambiguationData":[OSD([sQuery(id+"F0.wireOp",EDGE,"E34.filletArc")])],"isStart":true});
            var Q126;
            Q126=makeQuery(id+"F1.opExtrude","SWEPT_EDGE",EDGE,{"disambiguationData":[OSD([sQuery(id+"F0.wireOp",EDGE,"E26"),sQuery(id+"F0.wireOp",EDGE,"E34.filletArc")])]});
            var Q127;
            Q127=makeQuery(id+"F1.opExtrude","SWEPT_EDGE",EDGE,{"disambiguationData":[OSD([sQuery(id+"F0.wireOp",EDGE,"E29.trimOffspring"),sQuery(id+"F0.wireOp",EDGE,"E34.filletArc")])]});
            var Q128;
            Q128=makeQuery(id+"F1.opExtrude","SWEPT_EDGE",EDGE,{"disambiguationData":[OSD([sQuery(id+"F0.wireOp",EDGE,"E39.MirrorCS"),sQuery(id+"F0.wireOp",EDGE,"E42")])]});
            var Q129;
            Q129=makeQuery(id+"F1.opExtrude","CAP_EDGE",EDGE,{"disambiguationData":[OSD([sQuery(id+"F0.wireOp",EDGE,"E44.filletArc")])],"isStart":true});
            var Q130;
            Q130=makeQuery(id+"F1.opExtrude","CAP_EDGE",EDGE,{"disambiguationData":[OSD([sQuery(id+"F0.wireOp",EDGE,"E31.filletArc")])],"isStart":true});
            var Q131;
            Q131=makeQuery(id+"F1.opExtrude","SWEPT_EDGE",EDGE,{"disambiguationData":[OSD([sQuery(id+"F0.wireOp",EDGE,"E22"),sQuery(id+"F0.wireOp",EDGE,"E31.filletArc")])]});
            var Q132;
            Q132=makeQuery(id+"F1.opExtrude","CAP_EDGE",EDGE,{"disambiguationData":[OSD([sQuery(id+"F0.wireOp",EDGE,"E31.filletArc")])],"isStart":false});
            var Q133;
            Q133=makeQuery(id+"F1.opExtrude","CAP_EDGE",EDGE,{"disambiguationData":[OSD([sQuery(id+"F0.wireOp",EDGE,"E37.filletArc")])],"isStart":true});
            var Q134;
            Q134=makeQuery(id+"F1.opExtrude","SWEPT_EDGE",EDGE,{"disambiguationData":[OSD([sQuery(id+"F0.wireOp",EDGE,"E28.trimOffspring"),sQuery(id+"F0.wireOp",EDGE,"E31.filletArc")])]});
            fillet(context, id + "F2", {"entities" : qUnion([Q0, Q1, Q2, Q3, Q4, Q5, Q6, Q7, Q8, Q9, Q10, Q11, Q12, Q13, Q14, Q15, Q16, Q17, Q18, Q19, Q20, Q21, Q22, Q23, Q24, Q25, Q26, Q27, Q28, Q29, Q30, Q31, Q32, Q33, Q34, Q35, Q36, Q37, Q38, Q39, Q40, Q41, Q42, Q43, Q44, Q45, Q46, Q47, Q48, Q49, Q50, Q51, Q52, Q53, Q54, Q55, Q56, Q57, Q58, Q59, Q60, Q61, Q62, Q63, Q64, Q65, Q66, Q67, Q68, Q69, Q70, Q71, Q72, Q73, Q74, Q75, Q76, Q77, Q78, Q79, Q80, Q81, Q82, Q83, Q84, Q85, Q86, Q87, Q88, Q89, Q90, Q91, Q92, Q93, Q94, Q95, Q96, Q97, Q98, Q99, Q100, Q101, Q102, Q103, Q104, Q105, Q106, Q107, Q108, Q109, Q110, Q111, Q112, Q113, Q114, Q115, Q116, Q117, Q118, Q119, Q120, Q121, Q122, Q123, Q124, Q125, Q126, Q127, Q128, Q129, Q130, Q131, Q132, Q133, Q134]), "radius" : 1 * mm, "tangentPropagation" : true, "allowEdgeOverflow" : false});
        }
    });
